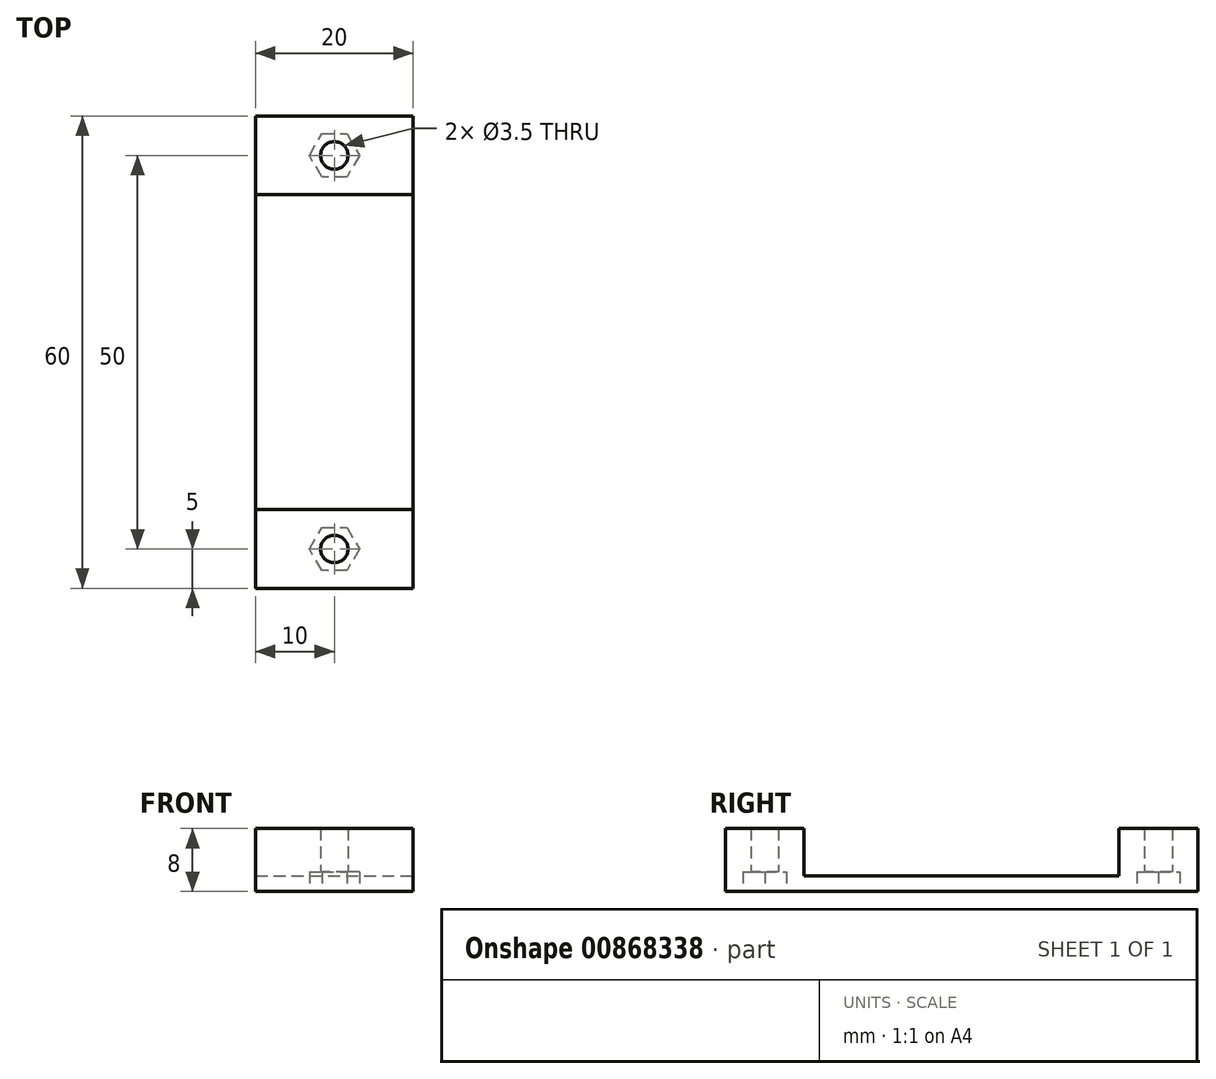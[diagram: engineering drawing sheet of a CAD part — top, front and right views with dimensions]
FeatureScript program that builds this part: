
annotation { "Feature Type Name" : "Feature", "Feature Type Description" : "" }
export const myFeature = defineFeature(function(context is Context, id is Id, definition is map)
    precondition{}
    {
        {
            var Q0;
            Q0=qCreatedBy(makeId("Top.planeOp"),FACE);
            var sketch = newSketch(context, id + "F0", { "sketchPlane" : qUnion([Q0])});
            skLineSegment(sketch, "E0.bottom", {"start": v(10, -30) * mm, "end": v(-10, -30) * mm});
            skLineSegment(sketch, "E0.top", {"start": v(10, 30) * mm, "end": v(-10, 30) * mm});
            skLineSegment(sketch, "E0.left", {"start": v(10, -30) * mm, "end": v(10, 30) * mm});
            skLineSegment(sketch, "E0.right", {"start": v(-10, -30) * mm, "end": v(-10, 30) * mm});
            skPoint(sketch, "E0.middle", {"position": v(0, 0) * mm});
            skCircle(sketch, "E1", {"center": v(0, 25) * mm, "radius": 1.75 * mm});
            skCircle(sketch, "E2.MirrorC", {"center": v(0, -25) * mm, "radius": 1.75 * mm});
            skSolve(sketch);
        }
        {
            var Q0;
            Q0 = qSketchRegion(id + "F0", true);
            extrude(context, id + "F1", {"entities" : qUnion([Q0]), "depth" : 2 * mm, "offsetDistance" : 25 * mm});
        }
        {
            var Q0;
            Q0=makeQuery(id+"F1.opExtrude","CAP_FACE",FACE,{"disambiguationData":[OSD([sQuery(id+"F0.wireOp",EDGE,"E0.bottom"),sQuery(id+"F0.wireOp",EDGE,"E0.top"),sQuery(id+"F0.wireOp",EDGE,"E0.left"),sQuery(id+"F0.wireOp",EDGE,"E0.right"),sQuery(id+"F0.wireOp",EDGE,"E1"),sQuery(id+"F0.wireOp",EDGE,"E2.MirrorC")])],"isStart":false});
            var Q1;
            Q1=makeQuery(id+"F1.opExtrude","CAP_FACE",FACE,{"disambiguationData":[OSD([sQuery(id+"F0.wireOp",EDGE,"E0.bottom"),sQuery(id+"F0.wireOp",EDGE,"E0.top"),sQuery(id+"F0.wireOp",EDGE,"E0.left"),sQuery(id+"F0.wireOp",EDGE,"E0.right"),sQuery(id+"F0.wireOp",EDGE,"E1"),sQuery(id+"F0.wireOp",EDGE,"E2.MirrorC")])],"isStart":false});
            var sketch = newSketch(context, id + "F2", { "sketchPlane" : qUnion([Q0, Q1])});
            skLineSegment(sketch, "E3.bottom", {"start": v(-10, 30) * mm, "end": v(10, 30) * mm});
            skLineSegment(sketch, "E3.top", {"start": v(-10, 20) * mm, "end": v(10, 20) * mm});
            skLineSegment(sketch, "E3.left", {"start": v(-10, 30) * mm, "end": v(-10, 20) * mm});
            skLineSegment(sketch, "E3.right", {"start": v(10, 30) * mm, "end": v(10, 20) * mm});
            skCircle(sketch, "E4", {"center": v(0, 25) * mm, "radius": 1.75 * mm});
            skLineSegment(sketch, "E5.MirrorCS", {"start": v(-10, -20) * mm, "end": v(10, -20) * mm});
            skLineSegment(sketch, "E6.MirrorCS", {"start": v(10, -30) * mm, "end": v(10, -20) * mm});
            skLineSegment(sketch, "E7.MirrorCS", {"start": v(-10, -30) * mm, "end": v(-10, -20) * mm});
            skLineSegment(sketch, "E8.MirrorCS", {"start": v(-10, -30) * mm, "end": v(10, -30) * mm});
            skCircle(sketch, "E9.MirrorC", {"center": v(0, -25) * mm, "radius": 1.75 * mm});
            skSolve(sketch);
        }
        {
            var Q0;
            Q0 = qSketchRegion(id + "F2", true);
            extrude(context, id + "F3", {"entities" : qUnion([Q0]), "operationType" : NewBodyOperationType.ADD, "depth" : 6 * mm, "offsetDistance" : 25 * mm});
        }
        {
            var Q0;
            Q0=makeQuery(id+"F0.imprint","IMPRINT",FACE,{"disambiguationData":[TD([[makeQuery(id+"F0.imprint","IMPRINT",EDGE,{"derivedFrom":sQuery(id+"F0.wireOp",EDGE,"E0.bottom")}),-1.0]])]});
            var Q1;
            Q1=makeQuery(id+"F0.imprint","IMPRINT",FACE,{"disambiguationData":[TD([[makeQuery(id+"F0.imprint","IMPRINT",EDGE,{"derivedFrom":sQuery(id+"F0.wireOp",EDGE,"E0.bottom")}),-1.0]])]});
            var Q2;
            Q2=makeQuery(id+"F0.imprint","IMPRINT",FACE,{"disambiguationData":[TD([[makeQuery(id+"F0.imprint","IMPRINT",EDGE,{"derivedFrom":sQuery(id+"F0.wireOp",EDGE,"E0.bottom")}),-1.0]])]});
            var sketch = newSketch(context, id + "F4", { "sketchPlane" : qUnion([Q0, Q1, Q2])});
            skCircle(sketch, "E10", {"center": v(0, -25) * mm, "radius": 2.75 * mm, "construction": true});
            skLineSegment(sketch, "E11.0", {"start": v(-1.59, -22.25) * mm, "end": v(1.59, -22.25) * mm});
            skLineSegment(sketch, "E11.1", {"start": v(1.59, -22.25) * mm, "end": v(3.18, -25) * mm});
            skLineSegment(sketch, "E11.2", {"start": v(3.18, -25) * mm, "end": v(1.59, -27.75) * mm});
            skLineSegment(sketch, "E11.3", {"start": v(1.59, -27.75) * mm, "end": v(-1.59, -27.75) * mm});
            skLineSegment(sketch, "E11.4", {"start": v(-1.59, -27.75) * mm, "end": v(-3.18, -25) * mm});
            skLineSegment(sketch, "E11.5", {"start": v(-3.18, -25) * mm, "end": v(-1.59, -22.25) * mm});
            skPoint(sketch, "E11.0.midPoint", {"position": v(0, -22.25) * mm});
            skCircle(sketch, "E12", {"center": v(0, 25) * mm, "radius": 2.75 * mm, "construction": true});
            skLineSegment(sketch, "E13.0", {"start": v(-1.59, 27.75) * mm, "end": v(1.59, 27.75) * mm});
            skLineSegment(sketch, "E13.1", {"start": v(1.59, 27.75) * mm, "end": v(3.18, 25) * mm});
            skLineSegment(sketch, "E13.2", {"start": v(3.18, 25) * mm, "end": v(1.59, 22.25) * mm});
            skLineSegment(sketch, "E13.3", {"start": v(1.59, 22.25) * mm, "end": v(-1.59, 22.25) * mm});
            skLineSegment(sketch, "E13.4", {"start": v(-1.59, 22.25) * mm, "end": v(-3.18, 25) * mm});
            skLineSegment(sketch, "E13.5", {"start": v(-3.18, 25) * mm, "end": v(-1.59, 27.75) * mm});
            skPoint(sketch, "E13.0.midPoint", {"position": v(0, 27.75) * mm});
            skSolve(sketch);
        }
        {
            var Q0;
            Q0 = qSketchRegion(id + "F4", true);
            extrude(context, id + "F5", {"entities" : qUnion([Q0]), "operationType" : NewBodyOperationType.REMOVE, "depth" : 2.5 * mm, "offsetDistance" : 25 * mm});
        }
    });
